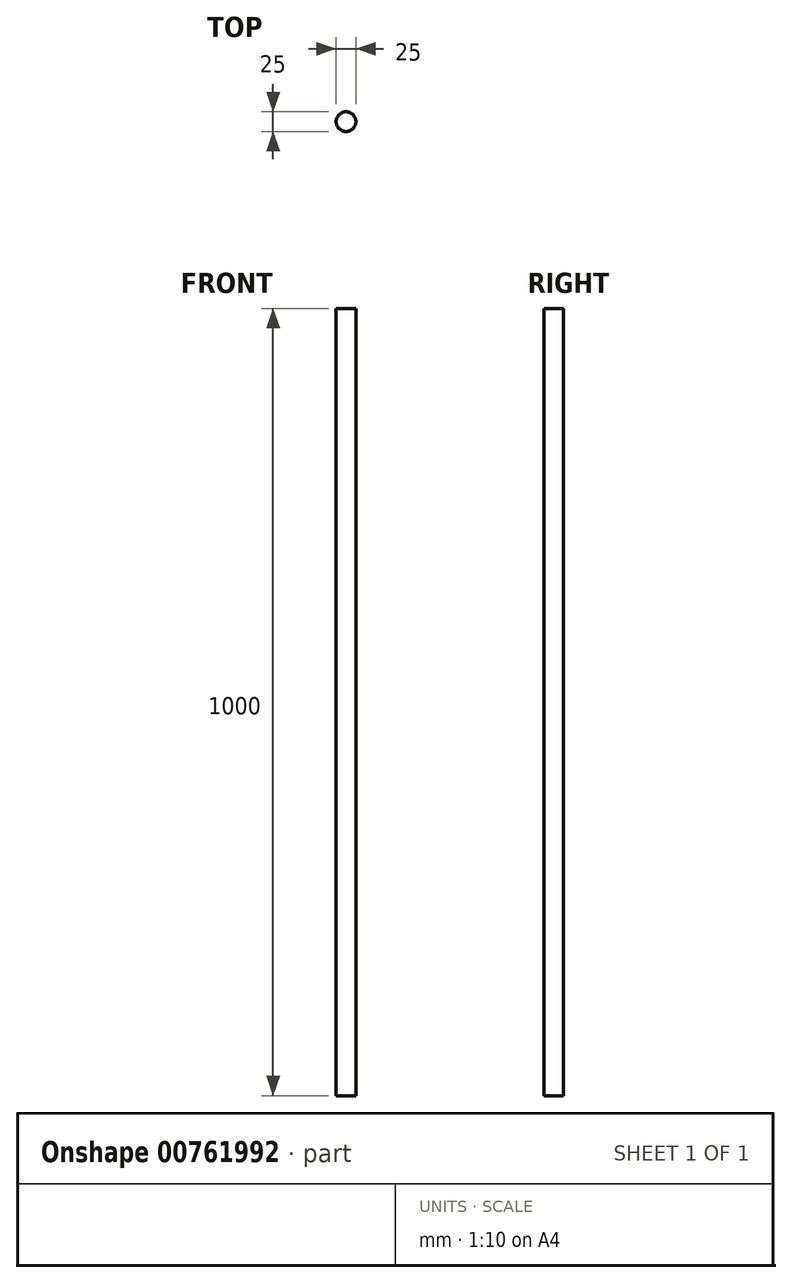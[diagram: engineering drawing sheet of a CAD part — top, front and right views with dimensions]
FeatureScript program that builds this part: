
annotation { "Feature Type Name" : "Feature", "Feature Type Description" : "" }
export const myFeature = defineFeature(function(context is Context, id is Id, definition is map)
    precondition{}
    {
        {
            var Q0;
            Q0=qCreatedBy(makeId("Top.planeOp"),FACE);
            var sketch = newSketch(context, id + "F0", { "sketchPlane" : qUnion([Q0])});
            skCircle(sketch, "E0", {"center": v(0, 0) * mm, "radius": 12.5 * mm});
            skSolve(sketch);
        }
        {
            var Q0;
            Q0=makeQuery(id+"F0.imprint","IMPRINT",FACE,{"disambiguationData":[TD([[makeQuery(id+"F0.imprint","IMPRINT",EDGE,{"derivedFrom":sQuery(id+"F0.wireOp",EDGE,"E0")}),1.0]])]});
            extrude(context, id + "F1", {"entities" : qUnion([Q0]), "depth" : 1000 * mm, "offsetDistance" : 25 * mm});
        }
    });
